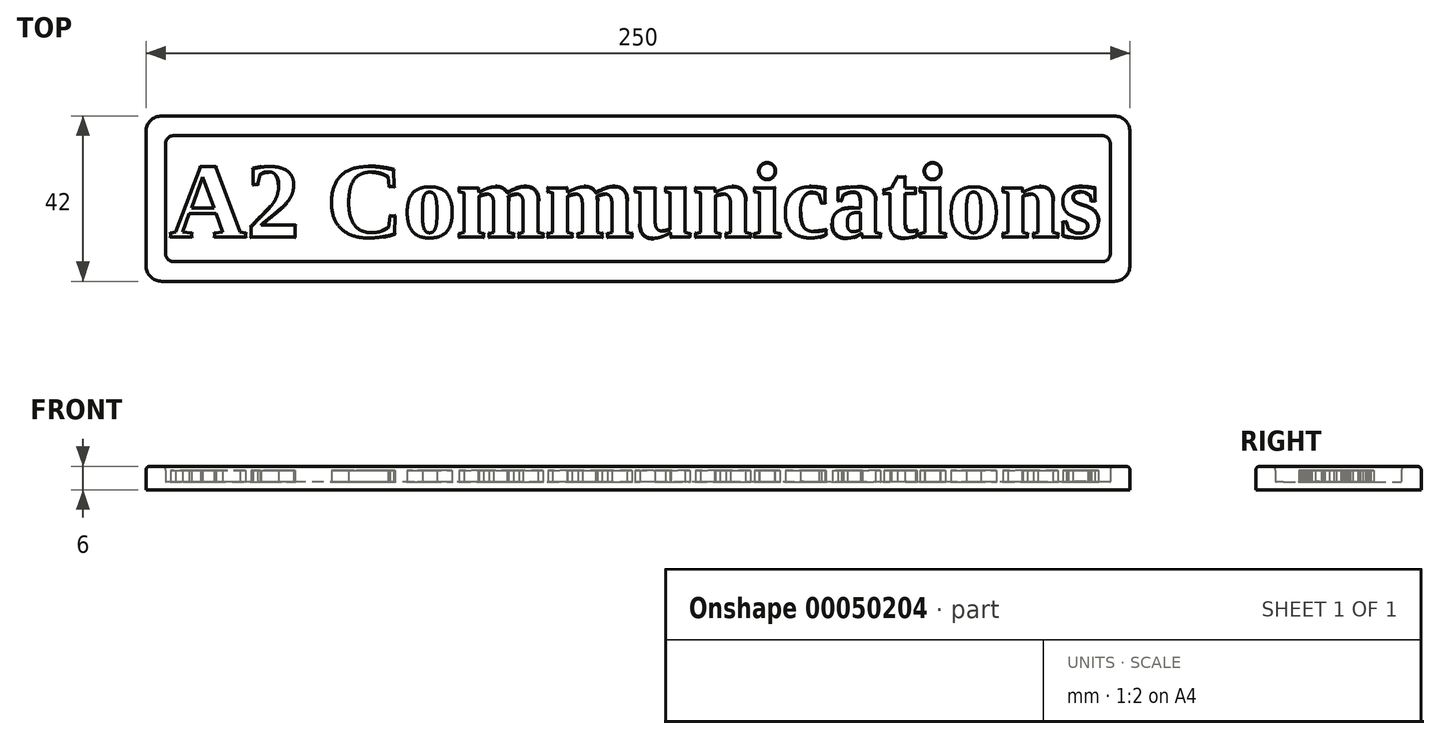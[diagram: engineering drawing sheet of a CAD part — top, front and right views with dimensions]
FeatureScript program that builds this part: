
annotation { "Feature Type Name" : "Feature", "Feature Type Description" : "" }
export const myFeature = defineFeature(function(context is Context, id is Id, definition is map)
    precondition{}
    {
        {
            var Q0;
            Q0=qCreatedBy(makeId("Top.planeOp"),FACE);
            var sketch = newSketch(context, id + "F0", { "sketchPlane" : qUnion([Q0])});
            skLineSegment(sketch, "E0.bottom", {"start": v(-125, 21) * mm, "end": v(125, 21) * mm});
            skLineSegment(sketch, "E0.top", {"start": v(-125, -21) * mm, "end": v(125, -21) * mm});
            skLineSegment(sketch, "E0.left", {"start": v(-125, 21) * mm, "end": v(-125, -21) * mm});
            skLineSegment(sketch, "E0.right", {"start": v(125, 21) * mm, "end": v(125, -21) * mm});
            skLineSegment(sketch, "E1.bottom", {"start": v(-120, 16) * mm, "end": v(120, 16) * mm});
            skLineSegment(sketch, "E1.top", {"start": v(-120, -16) * mm, "end": v(120, -16) * mm});
            skLineSegment(sketch, "E1.left", {"start": v(-120, 16) * mm, "end": v(-120, -16) * mm});
            skLineSegment(sketch, "E1.right", {"start": v(120, 16) * mm, "end": v(120, -16) * mm});
            skText(sketch, "E2", { "text": "A2 Communications", "fontName": "Tinos-Bold.ttf"});
            skLineSegment(sketch, "E3", {"start": v(-119, 0) * mm, "end": v(117, 0) * mm, "construction": true});
            const initialGuessF0  = {"E2": [-0.119, -0.00974, 1, 0, 0.01947]};
            skSetInitialGuess(sketch, initialGuessF0);
            skSolve(sketch);
        }
        {
            var Q0;
            Q0 = qSketchRegion(id + "F0", true);
            var Q1;
            {var subQ2=sQuery(id+"F0.wireOp",EDGE,"E1.bottom");Q1=makeQuery(id+"F0.imprint","IMPRINT",FACE,{"disambiguationData":[TD([[makeQuery(id+"F0.imprint","IMPRINT",EDGE,{"derivedFrom":subQ2}),-1.0]])]});}
            var Q2;
            Q2=makeQuery(id+"F0.imprint","IMPRINT",FACE,{"disambiguationData":[TD([[makeQuery(id+"F0.imprint","IMPRINT",EDGE,{"derivedFrom":sQuery(id+"F0.wireOp",EDGE,"E2.sketch_text.stroke-16")}),1.0]])]});
            var Q3;
            Q3=makeQuery(id+"F0.imprint","IMPRINT",FACE,{"disambiguationData":[TD([[makeQuery(id+"F0.imprint","IMPRINT",EDGE,{"derivedFrom":sQuery(id+"F0.wireOp",EDGE,"E2.sketch_text.stroke-0")}),-1.0]])]});
            var Q4;
            Q4=makeQuery(id+"F0.imprint","IMPRINT",FACE,{"disambiguationData":[TD([[makeQuery(id+"F0.imprint","IMPRINT",EDGE,{"derivedFrom":sQuery(id+"F0.wireOp",EDGE,"E2.sketch_text.stroke-19")}),-1.0]])]});
            var Q5;
            Q5=makeQuery(id+"F0.imprint","IMPRINT",FACE,{"disambiguationData":[TD([[makeQuery(id+"F0.imprint","IMPRINT",EDGE,{"derivedFrom":sQuery(id+"F0.wireOp",EDGE,"E2.sketch_text.stroke-42")}),-1.0]])]});
            var Q6;
            Q6=makeQuery(id+"F0.imprint","IMPRINT",FACE,{"disambiguationData":[TD([[makeQuery(id+"F0.imprint","IMPRINT",EDGE,{"derivedFrom":sQuery(id+"F0.wireOp",EDGE,"E2.sketch_text.stroke-62")}),-1.0]])]});
            var Q7;
            Q7=makeQuery(id+"F0.imprint","IMPRINT",FACE,{"disambiguationData":[TD([[makeQuery(id+"F0.imprint","IMPRINT",EDGE,{"derivedFrom":sQuery(id+"F0.wireOp",EDGE,"E2.sketch_text.stroke-70")}),1.0]])]});
            var Q8;
            Q8=makeQuery(id+"F0.imprint","IMPRINT",FACE,{"disambiguationData":[TD([[makeQuery(id+"F0.imprint","IMPRINT",EDGE,{"derivedFrom":sQuery(id+"F0.wireOp",EDGE,"E2.sketch_text.stroke-78")}),-1.0]])]});
            var Q9;
            Q9=makeQuery(id+"F0.imprint","IMPRINT",FACE,{"disambiguationData":[TD([[makeQuery(id+"F0.imprint","IMPRINT",EDGE,{"derivedFrom":sQuery(id+"F0.wireOp",EDGE,"E2.sketch_text.stroke-115")}),-1.0]])]});
            var Q10;
            Q10=makeQuery(id+"F0.imprint","IMPRINT",FACE,{"disambiguationData":[TD([[makeQuery(id+"F0.imprint","IMPRINT",EDGE,{"derivedFrom":sQuery(id+"F0.wireOp",EDGE,"E2.sketch_text.stroke-152")}),-1.0]])]});
            var Q11;
            Q11=makeQuery(id+"F0.imprint","IMPRINT",FACE,{"disambiguationData":[TD([[makeQuery(id+"F0.imprint","IMPRINT",EDGE,{"derivedFrom":sQuery(id+"F0.wireOp",EDGE,"E2.sketch_text.stroke-172")}),-1.0]])]});
            var Q12;
            Q12=makeQuery(id+"F0.imprint","IMPRINT",FACE,{"disambiguationData":[TD([[makeQuery(id+"F0.imprint","IMPRINT",EDGE,{"derivedFrom":sQuery(id+"F0.wireOp",EDGE,"E2.sketch_text.stroke-196")}),-1.0]])]});
            var Q13;
            Q13=makeQuery(id+"F0.imprint","IMPRINT",FACE,{"disambiguationData":[TD([[makeQuery(id+"F0.imprint","IMPRINT",EDGE,{"derivedFrom":sQuery(id+"F0.wireOp",EDGE,"E2.sketch_text.stroke-214")}),-1.0]])]});
            var Q14;
            Q14=makeQuery(id+"F0.imprint","IMPRINT",FACE,{"disambiguationData":[TD([[makeQuery(id+"F0.imprint","IMPRINT",EDGE,{"derivedFrom":sQuery(id+"F0.wireOp",EDGE,"E2.sketch_text.stroke-206")}),-1.0]])]});
            var Q15;
            Q15=makeQuery(id+"F0.imprint","IMPRINT",FACE,{"disambiguationData":[TD([[makeQuery(id+"F0.imprint","IMPRINT",EDGE,{"derivedFrom":sQuery(id+"F0.wireOp",EDGE,"E2.sketch_text.stroke-234")}),-1.0]])]});
            var Q16;
            Q16=makeQuery(id+"F0.imprint","IMPRINT",FACE,{"disambiguationData":[TD([[makeQuery(id+"F0.imprint","IMPRINT",EDGE,{"derivedFrom":sQuery(id+"F0.wireOp",EDGE,"E2.sketch_text.stroke-255")}),1.0]])]});
            var Q17;
            Q17=makeQuery(id+"F0.imprint","IMPRINT",FACE,{"disambiguationData":[TD([[makeQuery(id+"F0.imprint","IMPRINT",EDGE,{"derivedFrom":sQuery(id+"F0.wireOp",EDGE,"E2.sketch_text.stroke-262")}),-1.0]])]});
            var Q18;
            Q18=makeQuery(id+"F0.imprint","IMPRINT",FACE,{"disambiguationData":[TD([[makeQuery(id+"F0.imprint","IMPRINT",EDGE,{"derivedFrom":sQuery(id+"F0.wireOp",EDGE,"E2.sketch_text.stroke-291")}),-1.0]])]});
            var Q19;
            Q19=makeQuery(id+"F0.imprint","IMPRINT",FACE,{"disambiguationData":[TD([[makeQuery(id+"F0.imprint","IMPRINT",EDGE,{"derivedFrom":sQuery(id+"F0.wireOp",EDGE,"E2.sketch_text.stroke-281")}),-1.0]])]});
            var Q20;
            Q20=makeQuery(id+"F0.imprint","IMPRINT",FACE,{"disambiguationData":[TD([[makeQuery(id+"F0.imprint","IMPRINT",EDGE,{"derivedFrom":sQuery(id+"F0.wireOp",EDGE,"E2.sketch_text.stroke-299")}),-1.0]])]});
            var Q21;
            Q21=makeQuery(id+"F0.imprint","IMPRINT",FACE,{"disambiguationData":[TD([[makeQuery(id+"F0.imprint","IMPRINT",EDGE,{"derivedFrom":sQuery(id+"F0.wireOp",EDGE,"E2.sketch_text.stroke-315")}),-1.0]])]});
            var Q22;
            Q22=makeQuery(id+"F0.imprint","IMPRINT",FACE,{"disambiguationData":[TD([[makeQuery(id+"F0.imprint","IMPRINT",EDGE,{"derivedFrom":sQuery(id+"F0.wireOp",EDGE,"E2.sketch_text.stroke-339")}),-1.0]])]});
            var Q23;
            Q23=makeQuery(id+"F0.imprint","IMPRINT",FACE,{"disambiguationData":[TD([[makeQuery(id+"F0.imprint","IMPRINT",EDGE,{"derivedFrom":sQuery(id+"F0.wireOp",EDGE,"E2.sketch_text.stroke-307")}),1.0]])]});
            extrude(context, id + "F1", {"entities" : qUnion([Q0, Q1, Q2, Q3, Q4, Q5, Q6, Q7, Q8, Q9, Q10, Q11, Q12, Q13, Q14, Q15, Q16, Q17, Q18, Q19, Q20, Q21, Q22, Q23]), "depth" : 2 * mm});
        }
        {
            var Q0;
            Q0=makeQuery(id+"F0.imprint","IMPRINT",FACE,{"disambiguationData":[TD([[makeQuery(id+"F0.imprint","IMPRINT",EDGE,{"derivedFrom":sQuery(id+"F0.wireOp",EDGE,"E2.sketch_text.stroke-0")}),-1.0]])]});
            var Q1;
            Q1=makeQuery(id+"F0.imprint","IMPRINT",FACE,{"disambiguationData":[TD([[makeQuery(id+"F0.imprint","IMPRINT",EDGE,{"derivedFrom":sQuery(id+"F0.wireOp",EDGE,"E2.sketch_text.stroke-19")}),-1.0]])]});
            var Q2;
            Q2=makeQuery(id+"F0.imprint","IMPRINT",FACE,{"disambiguationData":[TD([[makeQuery(id+"F0.imprint","IMPRINT",EDGE,{"derivedFrom":sQuery(id+"F0.wireOp",EDGE,"E2.sketch_text.stroke-42")}),-1.0]])]});
            var Q3;
            Q3=makeQuery(id+"F0.imprint","IMPRINT",FACE,{"disambiguationData":[TD([[makeQuery(id+"F0.imprint","IMPRINT",EDGE,{"derivedFrom":sQuery(id+"F0.wireOp",EDGE,"E2.sketch_text.stroke-62")}),-1.0]])]});
            var Q4;
            Q4=makeQuery(id+"F0.imprint","IMPRINT",FACE,{"disambiguationData":[TD([[makeQuery(id+"F0.imprint","IMPRINT",EDGE,{"derivedFrom":sQuery(id+"F0.wireOp",EDGE,"E2.sketch_text.stroke-78")}),-1.0]])]});
            var Q5;
            Q5=makeQuery(id+"F0.imprint","IMPRINT",FACE,{"disambiguationData":[TD([[makeQuery(id+"F0.imprint","IMPRINT",EDGE,{"derivedFrom":sQuery(id+"F0.wireOp",EDGE,"E2.sketch_text.stroke-115")}),-1.0]])]});
            var Q6;
            Q6=makeQuery(id+"F0.imprint","IMPRINT",FACE,{"disambiguationData":[TD([[makeQuery(id+"F0.imprint","IMPRINT",EDGE,{"derivedFrom":sQuery(id+"F0.wireOp",EDGE,"E2.sketch_text.stroke-152")}),-1.0]])]});
            var Q7;
            Q7=makeQuery(id+"F0.imprint","IMPRINT",FACE,{"disambiguationData":[TD([[makeQuery(id+"F0.imprint","IMPRINT",EDGE,{"derivedFrom":sQuery(id+"F0.wireOp",EDGE,"E2.sketch_text.stroke-172")}),-1.0]])]});
            var Q8;
            Q8=makeQuery(id+"F0.imprint","IMPRINT",FACE,{"disambiguationData":[TD([[makeQuery(id+"F0.imprint","IMPRINT",EDGE,{"derivedFrom":sQuery(id+"F0.wireOp",EDGE,"E2.sketch_text.stroke-196")}),-1.0]])]});
            var Q9;
            Q9=makeQuery(id+"F0.imprint","IMPRINT",FACE,{"disambiguationData":[TD([[makeQuery(id+"F0.imprint","IMPRINT",EDGE,{"derivedFrom":sQuery(id+"F0.wireOp",EDGE,"E2.sketch_text.stroke-206")}),-1.0]])]});
            var Q10;
            Q10=makeQuery(id+"F0.imprint","IMPRINT",FACE,{"disambiguationData":[TD([[makeQuery(id+"F0.imprint","IMPRINT",EDGE,{"derivedFrom":sQuery(id+"F0.wireOp",EDGE,"E2.sketch_text.stroke-214")}),-1.0]])]});
            var Q11;
            Q11=makeQuery(id+"F0.imprint","IMPRINT",FACE,{"disambiguationData":[TD([[makeQuery(id+"F0.imprint","IMPRINT",EDGE,{"derivedFrom":sQuery(id+"F0.wireOp",EDGE,"E2.sketch_text.stroke-234")}),-1.0]])]});
            var Q12;
            Q12=makeQuery(id+"F0.imprint","IMPRINT",FACE,{"disambiguationData":[TD([[makeQuery(id+"F0.imprint","IMPRINT",EDGE,{"derivedFrom":sQuery(id+"F0.wireOp",EDGE,"E2.sketch_text.stroke-262")}),-1.0]])]});
            var Q13;
            Q13=makeQuery(id+"F0.imprint","IMPRINT",FACE,{"disambiguationData":[TD([[makeQuery(id+"F0.imprint","IMPRINT",EDGE,{"derivedFrom":sQuery(id+"F0.wireOp",EDGE,"E2.sketch_text.stroke-281")}),-1.0]])]});
            var Q14;
            Q14=makeQuery(id+"F0.imprint","IMPRINT",FACE,{"disambiguationData":[TD([[makeQuery(id+"F0.imprint","IMPRINT",EDGE,{"derivedFrom":sQuery(id+"F0.wireOp",EDGE,"E2.sketch_text.stroke-291")}),-1.0]])]});
            var Q15;
            Q15=makeQuery(id+"F0.imprint","IMPRINT",FACE,{"disambiguationData":[TD([[makeQuery(id+"F0.imprint","IMPRINT",EDGE,{"derivedFrom":sQuery(id+"F0.wireOp",EDGE,"E2.sketch_text.stroke-299")}),-1.0]])]});
            var Q16;
            Q16=makeQuery(id+"F0.imprint","IMPRINT",FACE,{"disambiguationData":[TD([[makeQuery(id+"F0.imprint","IMPRINT",EDGE,{"derivedFrom":sQuery(id+"F0.wireOp",EDGE,"E2.sketch_text.stroke-339")}),-1.0]])]});
            var Q17;
            Q17=makeQuery(id+"F0.imprint","IMPRINT",FACE,{"disambiguationData":[TD([[makeQuery(id+"F0.imprint","IMPRINT",EDGE,{"derivedFrom":sQuery(id+"F0.wireOp",EDGE,"E2.sketch_text.stroke-315")}),-1.0]])]});
            extrude(context, id + "F2", {"entities" : qUnion([Q0, Q1, Q2, Q3, Q4, Q5, Q6, Q7, Q8, Q9, Q10, Q11, Q12, Q13, Q14, Q15, Q16, Q17]), "operationType" : NewBodyOperationType.ADD, "depth" : 5 * mm});
        }
        {
            var Q0;
            Q0=makeQuery(id+"F0.imprint","IMPRINT",FACE,{"disambiguationData":[TD([[makeQuery(id+"F0.imprint","IMPRINT",EDGE,{"derivedFrom":sQuery(id+"F0.wireOp",EDGE,"E0.bottom")}),-1.0]])]});
            extrude(context, id + "F3", {"entities" : qUnion([Q0]), "operationType" : NewBodyOperationType.ADD, "depth" : 6 * mm});
        }
        {
            var Q0;
            {var subQ0=sQuery(id+"F0.wireOp",EDGE,"E0.left");var subQ1=sQuery(id+"F0.wireOp",EDGE,"E0.bottom");Q0=makeQuery(id+"F3.boolean.opBoolean","MERGE",EDGE,{"derivedFrom":[makeQuery(id+"F1.opExtrude","SWEPT_EDGE",EDGE,{"disambiguationData":[OSD([subQ1,subQ0])]}),makeQuery(id+"F3.opExtrude","SWEPT_EDGE",EDGE,{"disambiguationData":[OSD([subQ1,subQ0])]})]});}
            var Q1;
            {var subQ0=sQuery(id+"F0.wireOp",EDGE,"E0.left");var subQ1=sQuery(id+"F0.wireOp",EDGE,"E0.top");Q1=makeQuery(id+"F3.boolean.opBoolean","MERGE",EDGE,{"derivedFrom":[makeQuery(id+"F1.opExtrude","SWEPT_EDGE",EDGE,{"disambiguationData":[OSD([subQ1,subQ0])]}),makeQuery(id+"F3.opExtrude","SWEPT_EDGE",EDGE,{"disambiguationData":[OSD([subQ1,subQ0])]})]});}
            var Q2;
            {var subQ0=sQuery(id+"F0.wireOp",EDGE,"E0.right");var subQ1=sQuery(id+"F0.wireOp",EDGE,"E0.bottom");Q2=makeQuery(id+"F3.boolean.opBoolean","MERGE",EDGE,{"derivedFrom":[makeQuery(id+"F1.opExtrude","SWEPT_EDGE",EDGE,{"disambiguationData":[OSD([subQ1,subQ0])]}),makeQuery(id+"F3.opExtrude","SWEPT_EDGE",EDGE,{"disambiguationData":[OSD([subQ1,subQ0])]})]});}
            var Q3;
            {var subQ0=sQuery(id+"F0.wireOp",EDGE,"E0.right");var subQ1=sQuery(id+"F0.wireOp",EDGE,"E0.top");Q3=makeQuery(id+"F3.boolean.opBoolean","MERGE",EDGE,{"derivedFrom":[makeQuery(id+"F1.opExtrude","SWEPT_EDGE",EDGE,{"disambiguationData":[OSD([subQ1,subQ0])]}),makeQuery(id+"F3.opExtrude","SWEPT_EDGE",EDGE,{"disambiguationData":[OSD([subQ1,subQ0])]})]});}
            fillet(context, id + "F4", {"entities" : qUnion([Q0, Q1, Q2, Q3]), "radius" : 4 * mm, "tangentPropagation" : true, "allowEdgeOverflow" : false});
        }
        {
            var Q0;
            Q0=makeQuery(id+"F3.opExtrude","SWEPT_EDGE",EDGE,{"disambiguationData":[OSD([sQuery(id+"F0.wireOp",EDGE,"E1.bottom"),sQuery(id+"F0.wireOp",EDGE,"E1.left")])]});
            var Q1;
            Q1=makeQuery(id+"F3.opExtrude","SWEPT_EDGE",EDGE,{"disambiguationData":[OSD([sQuery(id+"F0.wireOp",EDGE,"E1.bottom"),sQuery(id+"F0.wireOp",EDGE,"E1.right")])]});
            var Q2;
            Q2=makeQuery(id+"F3.opExtrude","SWEPT_EDGE",EDGE,{"disambiguationData":[OSD([sQuery(id+"F0.wireOp",EDGE,"E1.top"),sQuery(id+"F0.wireOp",EDGE,"E1.right")])]});
            var Q3;
            Q3=makeQuery(id+"F3.opExtrude","SWEPT_EDGE",EDGE,{"disambiguationData":[OSD([sQuery(id+"F0.wireOp",EDGE,"E1.top"),sQuery(id+"F0.wireOp",EDGE,"E1.left")])]});
            fillet(context, id + "F5", {"entities" : qUnion([Q0, Q1, Q2, Q3]), "radius" : 2 * mm, "tangentPropagation" : true, "allowEdgeOverflow" : false});
        }
        {
            var Q0;
            Q0=makeQuery(id+"F3.opExtrude","CAP_FACE",FACE,{"disambiguationData":[OSD([sQuery(id+"F0.wireOp",EDGE,"E0.bottom"),sQuery(id+"F0.wireOp",EDGE,"E0.top"),sQuery(id+"F0.wireOp",EDGE,"E0.left"),sQuery(id+"F0.wireOp",EDGE,"E0.right"),sQuery(id+"F0.wireOp",EDGE,"E1.bottom"),sQuery(id+"F0.wireOp",EDGE,"E1.top"),sQuery(id+"F0.wireOp",EDGE,"E1.left"),sQuery(id+"F0.wireOp",EDGE,"E1.right")])],"isStart":false});
            fillet(context, id + "F6", {"entities" : qUnion([Q0]), "radius" : 1 * mm, "tangentPropagation" : true, "allowEdgeOverflow" : false});
        }
        {
            var Q0;
            {var subQ0=sQuery(id+"F0.wireOp",EDGE,"E0.left");var subQ1=sQuery(id+"F0.wireOp",EDGE,"E0.top");var subQ2=sQuery(id+"F0.wireOp",EDGE,"E0.bottom");var subQ3=sQuery(id+"F0.wireOp",EDGE,"E0.right");Q0=makeQuery(id+"F2.boolean.opBoolean","SPLIT",FACE,{"disambiguationData":[TD([makeQuery(id+"F1.opExtrude","SWEPT_FACE",FACE,{"disambiguationData":[OSD([subQ2])]})])],"derivedFrom":makeQuery(id+"F1.opExtrude","CAP_FACE",FACE,{"disambiguationData":[OSD([subQ2,subQ1,subQ0,subQ3])],"isStart":false})});}
            fillet(context, id + "F7", {"entities" : qUnion([Q0]), "radius" : 0.15 * mm, "tangentPropagation" : true, "allowEdgeOverflow" : false});
        }
    });
